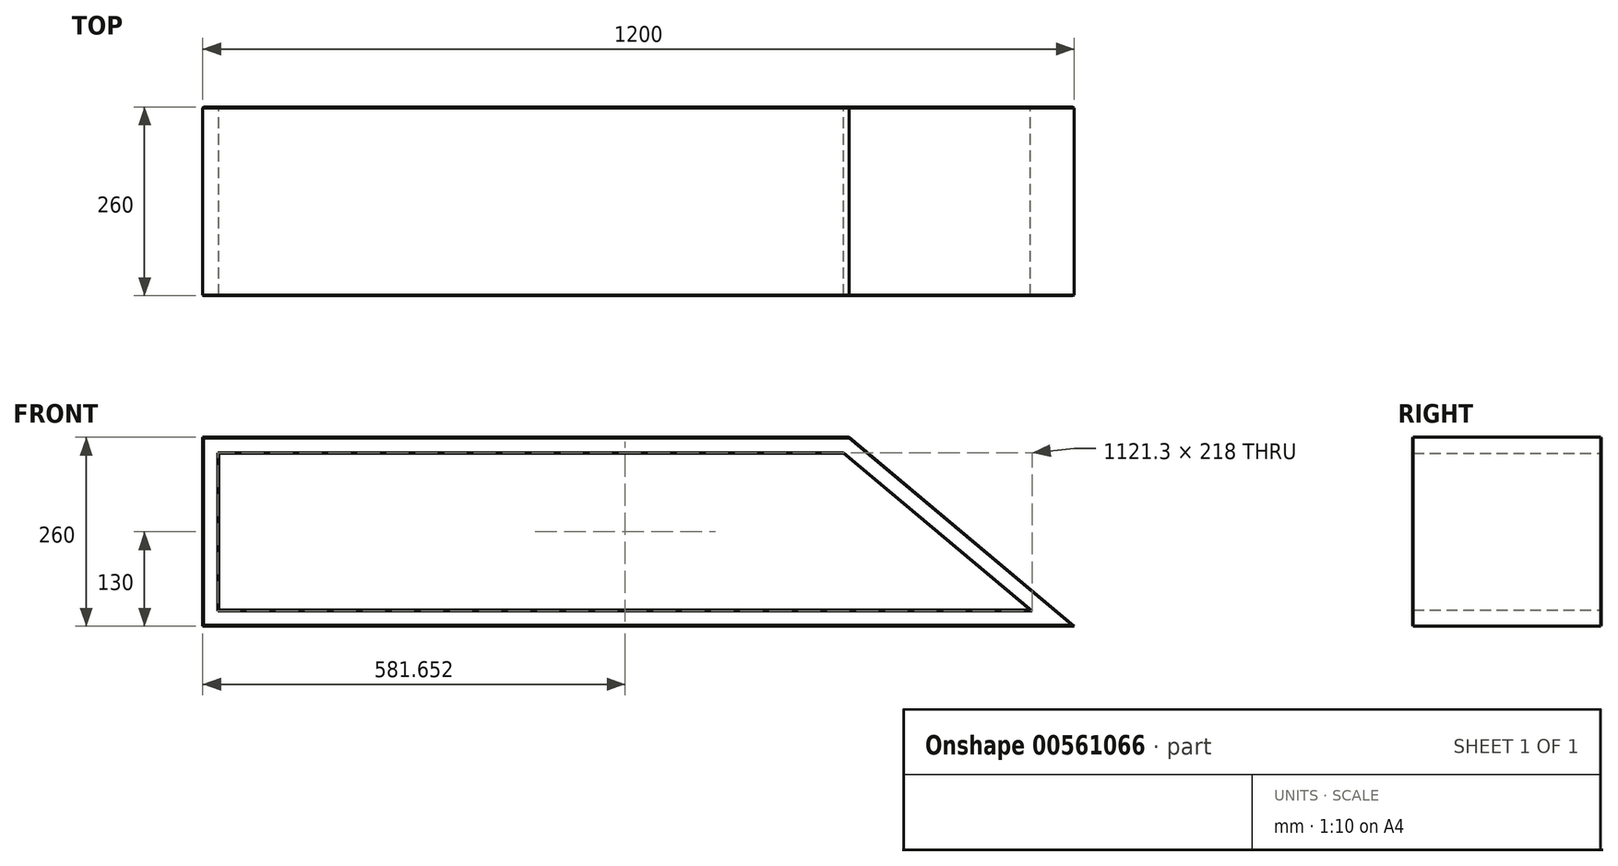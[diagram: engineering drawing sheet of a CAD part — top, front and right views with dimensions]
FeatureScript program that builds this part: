
annotation { "Feature Type Name" : "Feature", "Feature Type Description" : "" }
export const myFeature = defineFeature(function(context is Context, id is Id, definition is map)
    precondition{}
    {
        {
            var Q0;
            Q0=qCreatedBy(makeId("Front.planeOp"),FACE);
            var sketch = newSketch(context, id + "F0", { "sketchPlane" : qUnion([Q0])});
            skLineSegment(sketch, "E0", {"start": v(0, 0) * mm, "end": v(0, 260) * mm});
            skLineSegment(sketch, "E1", {"start": v(0, 260) * mm, "end": v(890.14, 260) * mm});
            skLineSegment(sketch, "E2", {"start": v(890.14, 260) * mm, "end": v(1200, 0) * mm});
            skLineSegment(sketch, "E3", {"start": v(1200, 0) * mm, "end": v(0, 0) * mm});
            skLineSegment(sketch, "E4.0", {"start": v(22, 238) * mm, "end": v(882.14, 238) * mm});
            skLineSegment(sketch, "E4.1", {"start": v(22, 22) * mm, "end": v(22, 238) * mm});
            skLineSegment(sketch, "E4.2", {"start": v(1139.56, 22) * mm, "end": v(22, 22) * mm});
            skLineSegment(sketch, "E4.3", {"start": v(882.14, 238) * mm, "end": v(1139.56, 22) * mm});
            skSolve(sketch);
        }
        {
            var Q0;
            Q0 = qSketchRegion(id + "F0", true);
            extrude(context, id + "F1", {"entities" : qUnion([Q0]), "depth" : 260 * mm, "offsetDistance" : 25 * mm});
        }
        {
            var Q0;
            Q0=makeQuery(id+"F1.opExtrude","CAP_EDGE",EDGE,{"disambiguationData":[OSD([sQuery(id+"F0.wireOp",EDGE,"E1")])],"isStart":false});
            var Q1;
            Q1=makeQuery(id+"F1.opExtrude","CAP_EDGE",EDGE,{"disambiguationData":[OSD([sQuery(id+"F0.wireOp",EDGE,"E4.0")])],"isStart":false});
            var Q2;
            Q2=makeQuery(id+"F1.opExtrude","CAP_EDGE",EDGE,{"disambiguationData":[OSD([sQuery(id+"F0.wireOp",EDGE,"E4.2")])],"isStart":false});
            var Q3;
            Q3=makeQuery(id+"F1.opExtrude","CAP_EDGE",EDGE,{"disambiguationData":[OSD([sQuery(id+"F0.wireOp",EDGE,"E3")])],"isStart":false});
            var Q4;
            Q4=makeQuery(id+"F1.opExtrude","CAP_EDGE",EDGE,{"disambiguationData":[OSD([sQuery(id+"F0.wireOp",EDGE,"E0")])],"isStart":false});
            var Q5;
            Q5=makeQuery(id+"F1.opExtrude","CAP_EDGE",EDGE,{"disambiguationData":[OSD([sQuery(id+"F0.wireOp",EDGE,"E4.1")])],"isStart":false});
            var Q6;
            Q6=makeQuery(id+"F1.opExtrude","CAP_EDGE",EDGE,{"disambiguationData":[OSD([sQuery(id+"F0.wireOp",EDGE,"E2")])],"isStart":false});
            var Q7;
            Q7=makeQuery(id+"F1.opExtrude","CAP_EDGE",EDGE,{"disambiguationData":[OSD([sQuery(id+"F0.wireOp",EDGE,"E4.3")])],"isStart":false});
            var Q8;
            Q8=makeQuery(id+"F1.opExtrude","CAP_EDGE",EDGE,{"disambiguationData":[OSD([sQuery(id+"F0.wireOp",EDGE,"E4.2")])],"isStart":true});
            var Q9;
            Q9=makeQuery(id+"F1.opExtrude","CAP_EDGE",EDGE,{"disambiguationData":[OSD([sQuery(id+"F0.wireOp",EDGE,"E1")])],"isStart":true});
            var Q10;
            Q10=makeQuery(id+"F1.opExtrude","CAP_EDGE",EDGE,{"disambiguationData":[OSD([sQuery(id+"F0.wireOp",EDGE,"E2")])],"isStart":true});
            var Q11;
            Q11=makeQuery(id+"F1.opExtrude","CAP_EDGE",EDGE,{"disambiguationData":[OSD([sQuery(id+"F0.wireOp",EDGE,"E4.3")])],"isStart":true});
            var Q12;
            Q12=makeQuery(id+"F1.opExtrude","CAP_EDGE",EDGE,{"disambiguationData":[OSD([sQuery(id+"F0.wireOp",EDGE,"E4.0")])],"isStart":true});
            var Q13;
            Q13=makeQuery(id+"F1.opExtrude","CAP_EDGE",EDGE,{"disambiguationData":[OSD([sQuery(id+"F0.wireOp",EDGE,"E0")])],"isStart":true});
            var Q14;
            Q14=makeQuery(id+"F1.opExtrude","CAP_EDGE",EDGE,{"disambiguationData":[OSD([sQuery(id+"F0.wireOp",EDGE,"E4.1")])],"isStart":true});
            var Q15;
            Q15=makeQuery(id+"F1.opExtrude","CAP_EDGE",EDGE,{"disambiguationData":[OSD([sQuery(id+"F0.wireOp",EDGE,"E3")])],"isStart":true});
            chamfer(context, id + "F2", {"entities" : qUnion([Q0, Q1, Q2, Q3, Q4, Q5, Q6, Q7, Q8, Q9, Q10, Q11, Q12, Q13, Q14, Q15]), "width" : 1 * mm, "tangentPropagation" : true});
        }
    });
